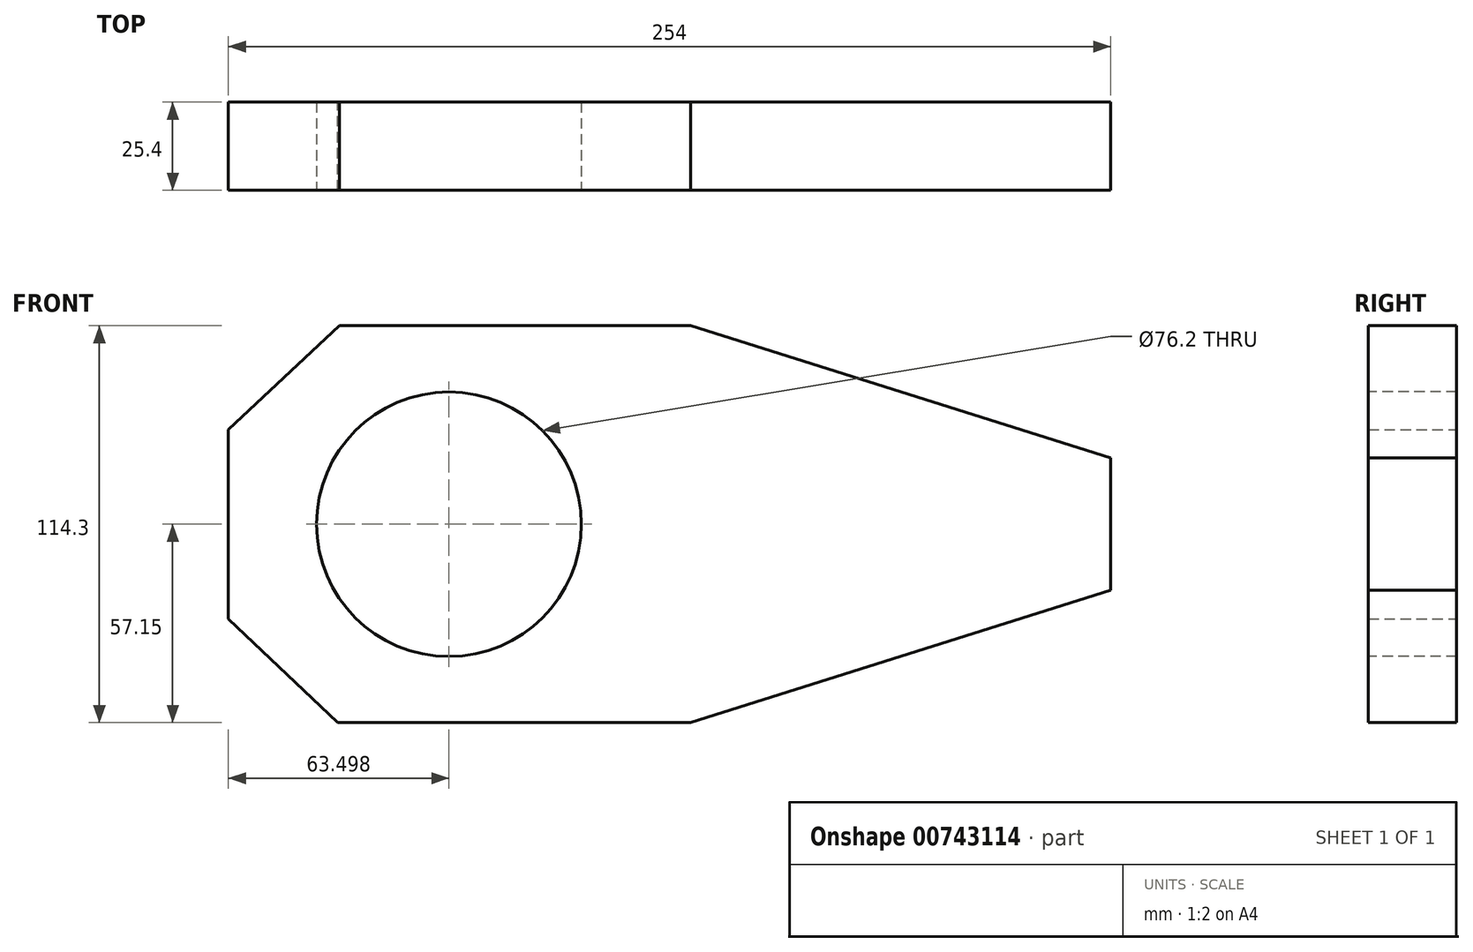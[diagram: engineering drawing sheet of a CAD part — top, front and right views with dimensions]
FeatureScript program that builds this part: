
annotation { "Feature Type Name" : "Feature", "Feature Type Description" : "" }
export const myFeature = defineFeature(function(context is Context, id is Id, definition is map)
    precondition{}
    {
        {
            var Q0;
            Q0=qCreatedBy(makeId("Front.planeOp"),FACE);
            var sketch = newSketch(context, id + "F0", { "sketchPlane" : qUnion([Q0])});
            skLineSegment(sketch, "E0", {"start": v(-45.05, 76.2) * mm, "end": v(-76.97, 46.34) * mm});
            skLineSegment(sketch, "E1", {"start": v(-76.97, 46.34) * mm, "end": v(-76.97, -8.24) * mm});
            skLineSegment(sketch, "E2", {"start": v(-76.97, -8.24) * mm, "end": v(-45.57, -38.1) * mm});
            skLineSegment(sketch, "E3", {"start": v(-45.57, -38.1) * mm, "end": v(56.03, -38.1) * mm});
            skLineSegment(sketch, "E4", {"start": v(56.03, -38.1) * mm, "end": v(177.03, 0) * mm});
            skLineSegment(sketch, "E5", {"start": v(177.03, 0) * mm, "end": v(177.03, 38.1) * mm});
            skLineSegment(sketch, "E6", {"start": v(177.03, 38.1) * mm, "end": v(56.03, 76.2) * mm});
            skLineSegment(sketch, "E7", {"start": v(56.03, 76.2) * mm, "end": v(-45.05, 76.2) * mm});
            skSolve(sketch);
        }
        {
            var Q0;
            Q0=makeQuery(id+"F0.imprint","IMPRINT",FACE,{"disambiguationData":[TD([[makeQuery(id+"F0.imprint","IMPRINT",EDGE,{"derivedFrom":sQuery(id+"F0.wireOp",EDGE,"E0")}),1.0]])]});
            extrude(context, id + "F1", {"entities" : qUnion([Q0]), "depth" : 25.4 * mm, "offsetDistance" : 25.4 * mm});
        }
        {
            var Q0;
            Q0=makeQuery(id+"F1.opExtrude","CAP_FACE",FACE,{"disambiguationData":[OSD([sQuery(id+"F0.wireOp",EDGE,"E0"),sQuery(id+"F0.wireOp",EDGE,"E1"),sQuery(id+"F0.wireOp",EDGE,"E2"),sQuery(id+"F0.wireOp",EDGE,"E3"),sQuery(id+"F0.wireOp",EDGE,"E4"),sQuery(id+"F0.wireOp",EDGE,"E5"),sQuery(id+"F0.wireOp",EDGE,"E6"),sQuery(id+"F0.wireOp",EDGE,"E7")])],"isStart":false});
            var sketch = newSketch(context, id + "F2", { "sketchPlane" : qUnion([Q0])});
            skCircle(sketch, "E8", {"center": v(-13.47, 19.05) * mm, "radius": 38.1 * mm});
            skSolve(sketch);
        }
        {
            var Q0;
            Q0=makeQuery(id+"F2.imprint","IMPRINT",FACE,{"disambiguationData":[TD([[makeQuery(id+"F2.imprint","IMPRINT",EDGE,{"derivedFrom":sQuery(id+"F2.wireOp",EDGE,"E8")}),1.0]])]});
            extrude(context, id + "F3", {"entities" : qUnion([Q0]), "operationType" : NewBodyOperationType.REMOVE, "oppositeDirection" : true, "depth" : 25.4 * mm, "offsetDistance" : 25.4 * mm});
        }
    });
